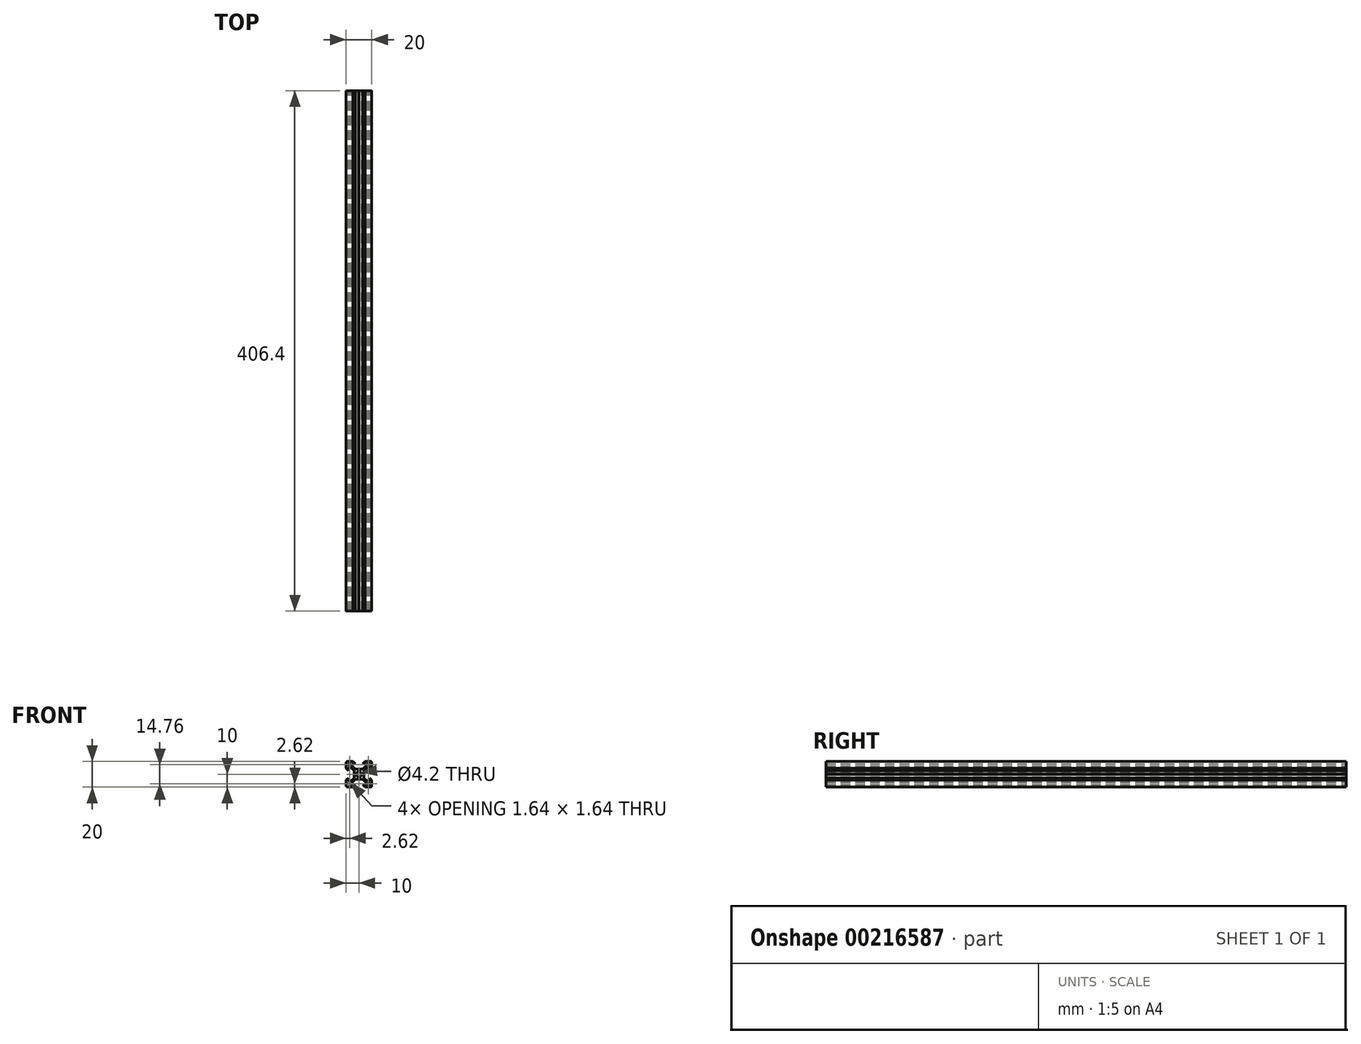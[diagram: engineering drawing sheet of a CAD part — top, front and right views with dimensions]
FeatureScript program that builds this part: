
annotation { "Feature Type Name" : "Feature", "Feature Type Description" : "" }
export const myFeature = defineFeature(function(context is Context, id is Id, definition is map)
    precondition{}
    {
        {
            var Q0;
            Q0=qCreatedBy(makeId("Front.planeOp"),FACE);
            var sketch = newSketch(context, id + "F0", { "sketchPlane" : qUnion([Q0])});
            skLineSegment(sketch, "E0.rect.bottom", {"start": v(-9, 10) * mm, "end": v(9, 10) * mm});
            skLineSegment(sketch, "E0.rect.top", {"start": v(-9, -10) * mm, "end": v(9, -10) * mm});
            skLineSegment(sketch, "E0.rect.left", {"start": v(-10, 9) * mm, "end": v(-10, -9) * mm});
            skLineSegment(sketch, "E0.rect.right", {"start": v(10, 9) * mm, "end": v(10, -9) * mm});
            skPoint(sketch, "E0.rect.middle", {"position": v(0, 0) * mm});
            skCircle(sketch, "E1", {"center": v(0, 0) * mm, "radius": 2.1 * mm});
            skPoint(sketch, "E2.visualSharp", {"position": v(-10, 10) * mm});
            skArc(sketch, "E2.filletArc", {"start": v(-9, 10) * mm, "mid": v(-9.7, 9.7) * mm, "end": v(-10, 9) * mm});
            skPoint(sketch, "E3.visualSharp", {"position": v(10, 10) * mm});
            skArc(sketch, "E3.filletArc", {"start": v(10, 9) * mm, "mid": v(9.7, 9.7) * mm, "end": v(9, 10) * mm});
            skPoint(sketch, "E4.visualSharp", {"position": v(10, -10) * mm});
            skArc(sketch, "E4.filletArc", {"start": v(9, -10) * mm, "mid": v(9.7, -9.7) * mm, "end": v(10, -9) * mm});
            skPoint(sketch, "E5.visualSharp", {"position": v(-10, -10) * mm});
            skArc(sketch, "E5.filletArc", {"start": v(-10, -9) * mm, "mid": v(-9.7, -9.7) * mm, "end": v(-9, -10) * mm});
            skLineSegment(sketch, "E6", {"start": v(10, 10) * mm, "end": v(-10, -10) * mm, "construction": true});
            skLineSegment(sketch, "E7", {"start": v(-10, 10) * mm, "end": v(10, -10) * mm, "construction": true});
            skLineSegment(sketch, "E8", {"start": v(-4.64, 10) * mm, "end": v(-2.84, 8.2) * mm});
            skLineSegment(sketch, "E9", {"start": v(-2.84, 8.2) * mm, "end": v(-5.5, 8.2) * mm});
            skLineSegment(sketch, "E10", {"start": v(-5.5, 8.2) * mm, "end": v(-5.5, 6.56) * mm});
            skLineSegment(sketch, "E11", {"start": v(-5.5, 6.56) * mm, "end": v(-2.84, 3.9) * mm});
            skLineSegment(sketch, "E12.MirrorCS", {"start": v(4.64, 10) * mm, "end": v(2.84, 8.2) * mm});
            skLineSegment(sketch, "E13.MirrorCS", {"start": v(2.84, 8.2) * mm, "end": v(5.5, 8.2) * mm});
            skLineSegment(sketch, "E14.MirrorCS", {"start": v(5.5, 8.2) * mm, "end": v(5.5, 6.56) * mm});
            skLineSegment(sketch, "E15.MirrorCS", {"start": v(5.5, 6.56) * mm, "end": v(2.84, 3.9) * mm});
            skLineSegment(sketch, "E16", {"start": v(-2.84, 3.9) * mm, "end": v(2.84, 3.9) * mm});
            skLineSegment(sketch, "E17.MirrorCS", {"start": v(-4.64, -10) * mm, "end": v(-2.84, -8.2) * mm});
            skLineSegment(sketch, "E18.MirrorCS", {"start": v(-2.84, -8.2) * mm, "end": v(-5.5, -8.2) * mm});
            skLineSegment(sketch, "E19.MirrorCS", {"start": v(-5.5, -8.2) * mm, "end": v(-5.5, -6.56) * mm});
            skLineSegment(sketch, "E20.MirrorCS", {"start": v(-5.5, -6.56) * mm, "end": v(-2.84, -3.9) * mm});
            skLineSegment(sketch, "E21.MirrorCS", {"start": v(-2.84, -3.9) * mm, "end": v(2.84, -3.9) * mm});
            skLineSegment(sketch, "E22.MirrorCS", {"start": v(5.5, -6.56) * mm, "end": v(2.84, -3.9) * mm});
            skLineSegment(sketch, "E23.MirrorCS", {"start": v(5.5, -8.2) * mm, "end": v(5.5, -6.56) * mm});
            skLineSegment(sketch, "E24.MirrorCS", {"start": v(2.84, -8.2) * mm, "end": v(5.5, -8.2) * mm});
            skLineSegment(sketch, "E25.MirrorCS", {"start": v(4.64, -10) * mm, "end": v(2.84, -8.2) * mm});
            skLineSegment(sketch, "E26.MirrorCS", {"start": v(10, -4.64) * mm, "end": v(8.2, -2.84) * mm});
            skLineSegment(sketch, "E27.MirrorCS", {"start": v(8.2, -2.84) * mm, "end": v(8.2, -5.5) * mm});
            skLineSegment(sketch, "E28.MirrorCS", {"start": v(8.2, -5.5) * mm, "end": v(6.56, -5.5) * mm});
            skLineSegment(sketch, "E29.MirrorCS", {"start": v(6.56, -5.5) * mm, "end": v(3.9, -2.84) * mm});
            skLineSegment(sketch, "E30.MirrorCS", {"start": v(3.9, -2.84) * mm, "end": v(3.9, 2.84) * mm});
            skLineSegment(sketch, "E31.MirrorCS", {"start": v(6.56, 5.5) * mm, "end": v(3.9, 2.84) * mm});
            skLineSegment(sketch, "E32.MirrorCS", {"start": v(8.2, 5.5) * mm, "end": v(6.56, 5.5) * mm});
            skLineSegment(sketch, "E33.MirrorCS", {"start": v(8.2, 2.84) * mm, "end": v(8.2, 5.5) * mm});
            skLineSegment(sketch, "E34.MirrorCS", {"start": v(10, 4.64) * mm, "end": v(8.2, 2.84) * mm});
            skLineSegment(sketch, "E35.MirrorCS", {"start": v(-8.2, 2.84) * mm, "end": v(-8.2, 5.5) * mm});
            skLineSegment(sketch, "E36.MirrorCS", {"start": v(-10, 4.64) * mm, "end": v(-8.2, 2.84) * mm});
            skLineSegment(sketch, "E37.MirrorCS", {"start": v(-8.2, 5.5) * mm, "end": v(-6.56, 5.5) * mm});
            skLineSegment(sketch, "E38.MirrorCS", {"start": v(-6.56, 5.5) * mm, "end": v(-3.9, 2.84) * mm});
            skLineSegment(sketch, "E39.MirrorCS", {"start": v(-3.9, 2.84) * mm, "end": v(-3.9, -2.84) * mm});
            skLineSegment(sketch, "E40.MirrorCS", {"start": v(-6.56, -5.5) * mm, "end": v(-3.9, -2.84) * mm});
            skLineSegment(sketch, "E41.MirrorCS", {"start": v(-8.2, -5.5) * mm, "end": v(-6.56, -5.5) * mm});
            skLineSegment(sketch, "E42.MirrorCS", {"start": v(-8.2, -2.84) * mm, "end": v(-8.2, -5.5) * mm});
            skLineSegment(sketch, "E43.MirrorCS", {"start": v(-10, -4.64) * mm, "end": v(-8.2, -2.84) * mm});
            skLineSegment(sketch, "E44", {"start": v(-8.05, 8.2) * mm, "end": v(-6.71, 8.2) * mm});
            skLineSegment(sketch, "E45", {"start": v(-6.56, 8.05) * mm, "end": v(-6.56, 8.05) * mm});
            skLineSegment(sketch, "E46", {"start": v(-6.6, 7.94) * mm, "end": v(-7.94, 6.6) * mm});
            skLineSegment(sketch, "E47", {"start": v(-8.05, 6.56) * mm, "end": v(-8.05, 6.56) * mm});
            skLineSegment(sketch, "E48", {"start": v(-8.2, 6.7) * mm, "end": v(-8.2, 8.05) * mm});
            skLineSegment(sketch, "E49.MirrorCS", {"start": v(8.2, 6.71) * mm, "end": v(8.2, 8.05) * mm});
            skLineSegment(sketch, "E50.MirrorCS", {"start": v(7.99, 6.56) * mm, "end": v(8.05, 6.56) * mm});
            skLineSegment(sketch, "E51.MirrorCS", {"start": v(6.56, 7.99) * mm, "end": v(7.99, 6.56) * mm});
            skLineSegment(sketch, "E52.MirrorCS", {"start": v(6.56, 8.05) * mm, "end": v(6.56, 7.99) * mm});
            skLineSegment(sketch, "E53.MirrorCS", {"start": v(8.05, 8.2) * mm, "end": v(6.7, 8.2) * mm});
            skLineSegment(sketch, "E54.MirrorCS", {"start": v(-8.2, -6.7) * mm, "end": v(-8.2, -8.2) * mm});
            skLineSegment(sketch, "E55.MirrorCS", {"start": v(-7.99, -6.56) * mm, "end": v(-8.05, -6.56) * mm});
            skLineSegment(sketch, "E56.MirrorCS", {"start": v(-6.6, -7.94) * mm, "end": v(-7.99, -6.56) * mm});
            skLineSegment(sketch, "E57.MirrorCS", {"start": v(-6.56, -8.05) * mm, "end": v(-6.56, -8.05) * mm});
            skLineSegment(sketch, "E58.MirrorCS", {"start": v(-8.2, -8.2) * mm, "end": v(-6.7, -8.2) * mm});
            skLineSegment(sketch, "E59.MirrorCS", {"start": v(6.56, -8.05) * mm, "end": v(6.56, -7.99) * mm});
            skLineSegment(sketch, "E60.MirrorCS", {"start": v(6.56, -7.99) * mm, "end": v(7.94, -6.6) * mm});
            skLineSegment(sketch, "E61.MirrorCS", {"start": v(8.05, -6.56) * mm, "end": v(8.2, -6.56) * mm});
            skLineSegment(sketch, "E62.MirrorCS", {"start": v(8.2, -6.56) * mm, "end": v(8.2, -8.05) * mm});
            skLineSegment(sketch, "E63.MirrorCS", {"start": v(8.05, -8.2) * mm, "end": v(6.7, -8.2) * mm});
            skLineSegment(sketch, "E64", {"start": v(-0.15, 3.9) * mm, "end": v(0, 3.75) * mm});
            skLineSegment(sketch, "E65", {"start": v(0, 3.75) * mm, "end": v(0.15, 3.9) * mm});
            skLineSegment(sketch, "E66.MirrorCS", {"start": v(-0.15, -3.9) * mm, "end": v(0, -3.75) * mm});
            skLineSegment(sketch, "E67.MirrorCS", {"start": v(0, -3.75) * mm, "end": v(0.15, -3.9) * mm});
            skLineSegment(sketch, "E68.MirrorCS", {"start": v(3.9, -0.15) * mm, "end": v(3.75, 0) * mm});
            skLineSegment(sketch, "E69.MirrorCS", {"start": v(3.75, 0) * mm, "end": v(3.9, 0.15) * mm});
            skLineSegment(sketch, "E70.MirrorCS", {"start": v(-3.9, 0.15) * mm, "end": v(-3.75, 0) * mm});
            skLineSegment(sketch, "E71.MirrorCS", {"start": v(-3.75, 0) * mm, "end": v(-3.9, -0.15) * mm});
            skPoint(sketch, "E72.visualSharp", {"position": v(-8.2, 8.2) * mm});
            skArc(sketch, "E72.filletArc", {"start": v(-8.05, 8.2) * mm, "mid": v(-8.16, 8.16) * mm, "end": v(-8.2, 8.05) * mm});
            skPoint(sketch, "E73.visualSharp", {"position": v(-6.56, 7.99) * mm});
            skArc(sketch, "E73.filletArc", {"start": v(-6.6, 7.94) * mm, "mid": v(-6.57, 8) * mm, "end": v(-6.56, 8.05) * mm});
            skPoint(sketch, "E74.visualSharp", {"position": v(-7.99, 6.56) * mm});
            skArc(sketch, "E74.filletArc", {"start": v(-8.05, 6.56) * mm, "mid": v(-8, 6.57) * mm, "end": v(-7.94, 6.6) * mm});
            skPoint(sketch, "E75.visualSharp", {"position": v(-6.56, 8.2) * mm});
            skArc(sketch, "E75.filletArc", {"start": v(-6.56, 8.05) * mm, "mid": v(-6.6, 8.16) * mm, "end": v(-6.71, 8.2) * mm});
            skPoint(sketch, "E76.visualSharp", {"position": v(-8.2, 6.56) * mm});
            skArc(sketch, "E76.filletArc", {"start": v(-8.2, 6.7) * mm, "mid": v(-8.16, 6.6) * mm, "end": v(-8.05, 6.56) * mm});
            skPoint(sketch, "E77.visualSharp", {"position": v(6.56, 8.2) * mm});
            skArc(sketch, "E77.filletArc", {"start": v(6.7, 8.2) * mm, "mid": v(6.6, 8.16) * mm, "end": v(6.56, 8.05) * mm});
            skPoint(sketch, "E78.visualSharp", {"position": v(8.2, 8.2) * mm});
            skArc(sketch, "E78.filletArc", {"start": v(8.2, 8.05) * mm, "mid": v(8.16, 8.16) * mm, "end": v(8.05, 8.2) * mm});
            skPoint(sketch, "E79.visualSharp", {"position": v(8.2, 6.56) * mm});
            skArc(sketch, "E79.filletArc", {"start": v(8.05, 6.56) * mm, "mid": v(8.16, 6.6) * mm, "end": v(8.2, 6.71) * mm});
            skPoint(sketch, "E80.visualSharp", {"position": v(6.56, -8.2) * mm});
            skArc(sketch, "E80.filletArc", {"start": v(6.56, -8.05) * mm, "mid": v(6.6, -8.16) * mm, "end": v(6.7, -8.2) * mm});
            skPoint(sketch, "E81.visualSharp", {"position": v(7.99, -6.56) * mm});
            skArc(sketch, "E81.filletArc", {"start": v(8.05, -6.56) * mm, "mid": v(8, -6.57) * mm, "end": v(7.94, -6.6) * mm});
            skPoint(sketch, "E82.visualSharp", {"position": v(8.2, -8.2) * mm});
            skArc(sketch, "E82.filletArc", {"start": v(8.05, -8.2) * mm, "mid": v(8.16, -8.16) * mm, "end": v(8.2, -8.05) * mm});
            skPoint(sketch, "E83.visualSharp", {"position": v(-6.56, -8.2) * mm});
            skArc(sketch, "E83.filletArc", {"start": v(-6.7, -8.2) * mm, "mid": v(-6.6, -8.16) * mm, "end": v(-6.56, -8.05) * mm});
            skPoint(sketch, "E84.visualSharp", {"position": v(-8.2, -6.56) * mm});
            skArc(sketch, "E84.filletArc", {"start": v(-8.05, -6.56) * mm, "mid": v(-8.16, -6.6) * mm, "end": v(-8.2, -6.7) * mm});
            skPoint(sketch, "E85.visualSharp", {"position": v(-6.56, -7.99) * mm});
            skArc(sketch, "E85.filletArc", {"start": v(-6.56, -8.05) * mm, "mid": v(-6.57, -8) * mm, "end": v(-6.6, -7.94) * mm});
            skSolve(sketch);
        }
        {
            var Q0;
            Q0=makeQuery(id+"F0.imprint","IMPRINT",FACE,{"disambiguationData":[TD([[makeQuery(id+"F0.imprint","IMPRINT",EDGE,{"derivedFrom":sQuery(id+"F0.wireOp",EDGE,"E1")}),-1.0]])]});
            extrude(context, id + "F1", {"entities" : qUnion([Q0]), "depth" : 406.4 * mm});
        }
    });
